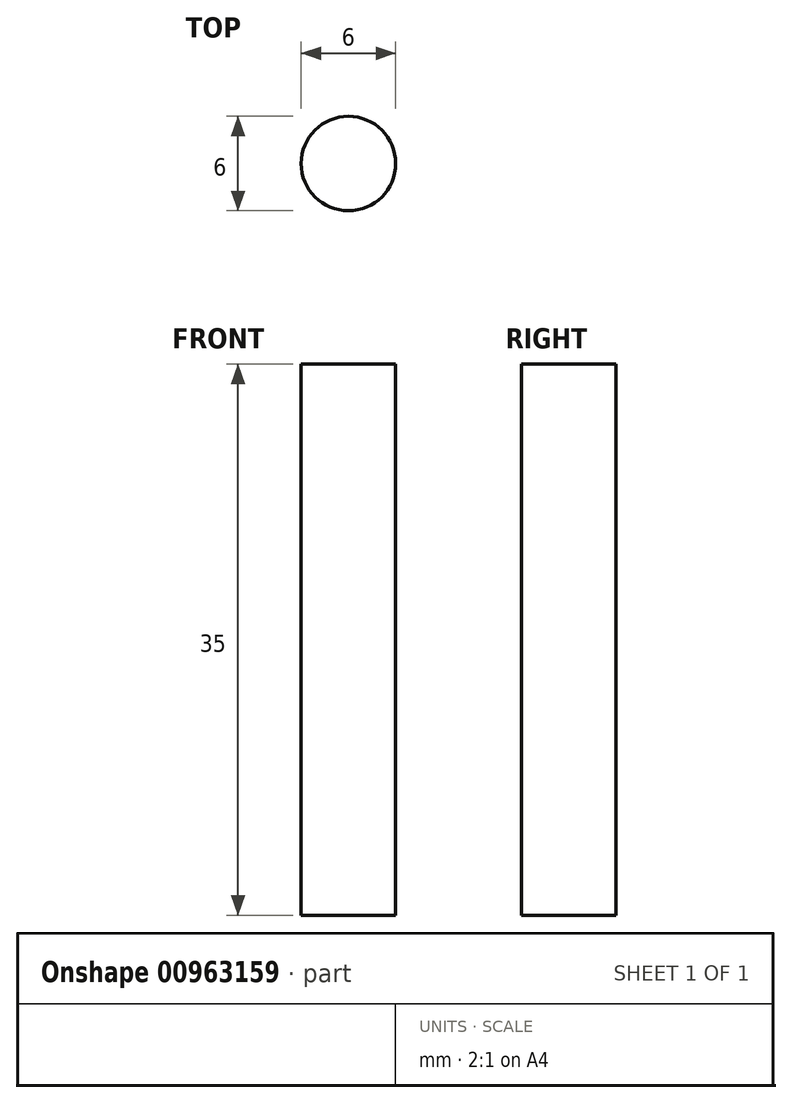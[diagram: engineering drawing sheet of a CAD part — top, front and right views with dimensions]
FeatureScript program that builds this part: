
annotation { "Feature Type Name" : "Feature", "Feature Type Description" : "" }
export const myFeature = defineFeature(function(context is Context, id is Id, definition is map)
    precondition{}
    {
        {
            var Q0;
            Q0=qCreatedBy(makeId("Top.planeOp"),FACE);
            var sketch = newSketch(context, id + "F0", { "sketchPlane" : qUnion([Q0])});
            skCircle(sketch, "E0", {"center": v(0, 0) * mm, "radius": 3 * mm});
            skSolve(sketch);
        }
        {
            var Q0;
            Q0=makeQuery(id+"F0.imprint","IMPRINT",FACE,{"disambiguationData":[TD([[makeQuery(id+"F0.imprint","IMPRINT",EDGE,{"derivedFrom":sQuery(id+"F0.wireOp",EDGE,"E0")}),1.0]])]});
            extrude(context, id + "F1", {"entities" : qUnion([Q0]), "depth" : 35 * mm, "offsetDistance" : 25 * mm});
        }
    });
